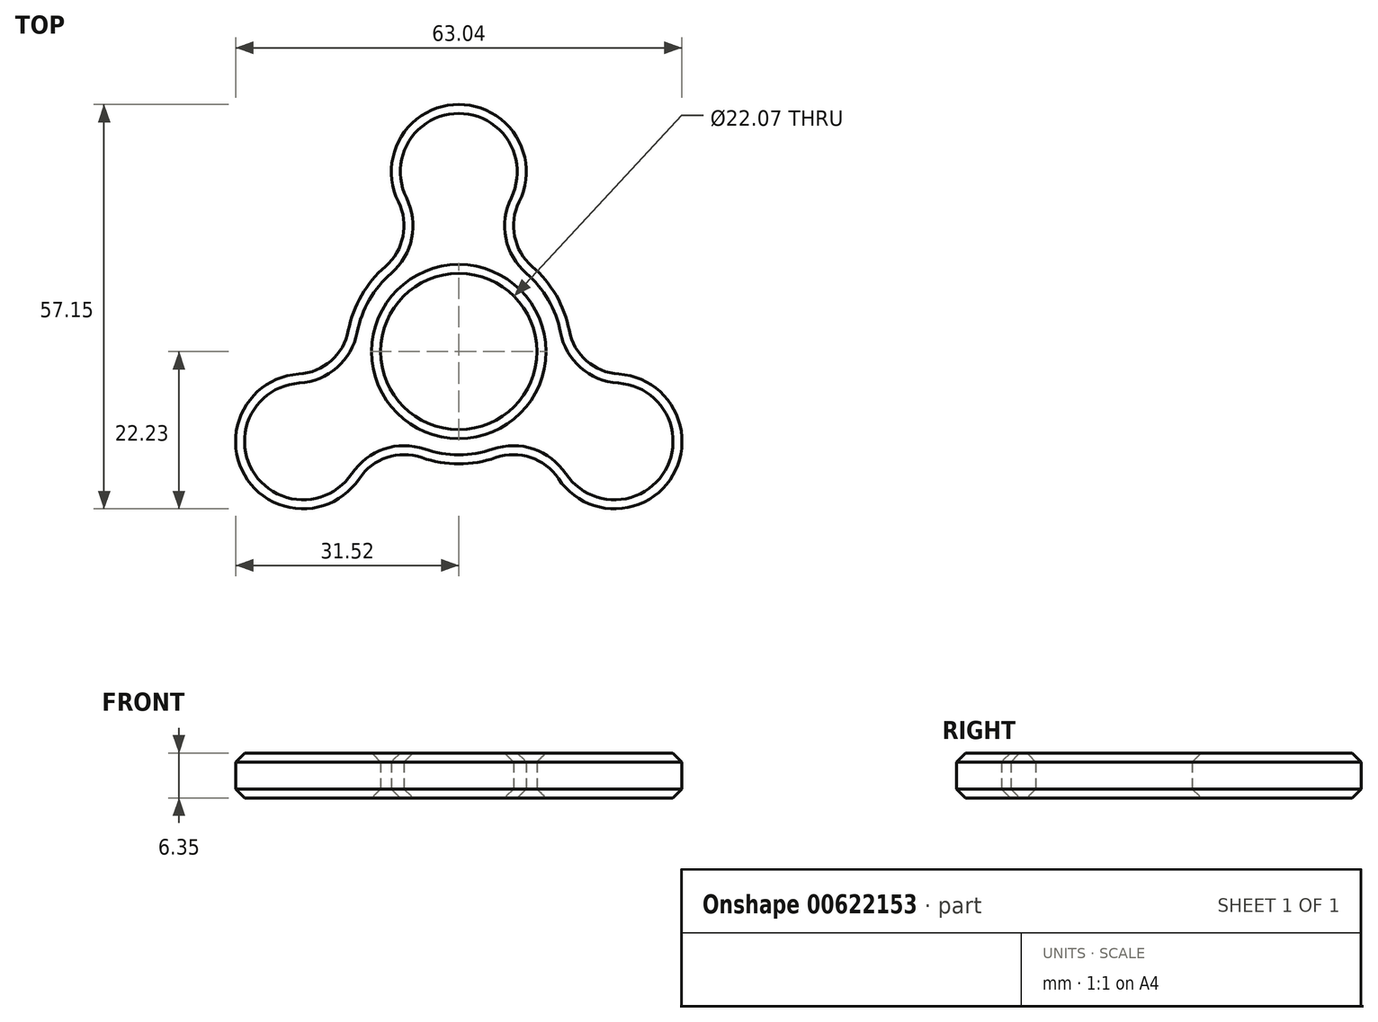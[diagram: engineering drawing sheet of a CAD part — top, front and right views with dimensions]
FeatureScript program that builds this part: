
annotation { "Feature Type Name" : "Feature", "Feature Type Description" : "" }
export const myFeature = defineFeature(function(context is Context, id is Id, definition is map)
    precondition{}
    {
        {
            var Q0;
            Q0=qCreatedBy(makeId("Top.planeOp"),FACE);
            var sketch = newSketch(context, id + "F0", { "sketchPlane" : qUnion([Q0])});
            skCircle(sketch, "E0", {"center": v(0, 0) * mm, "radius": 11.04 * mm});
            skCircle(sketch, "E1", {"center": v(0, 0) * mm, "radius": 15.88 * mm});
            skCircle(sketch, "E2", {"center": v(0, 25.4) * mm, "radius": 9.53 * mm});
            skCircle(sketch, "E3.1.0", {"center": v(-22, -12.7) * mm, "radius": 9.53 * mm});
            skCircle(sketch, "E3.2.0", {"center": v(22, -12.7) * mm, "radius": 9.53 * mm});
            skArc(sketch, "E4", {"start": v(-22.6, -3.2) * mm, "mid": v(-18.04, -1.3) * mm, "end": v(-15.6, 2.98) * mm});
            skArc(sketch, "E5", {"start": v(-5.22, -15) * mm, "mid": v(-10.15, -14.97) * mm, "end": v(-14.06, -17.97) * mm});
            skArc(sketch, "E6.1.0", {"start": v(14.06, -17.97) * mm, "mid": v(10.15, -14.97) * mm, "end": v(5.22, -15) * mm});
            skArc(sketch, "E6.1.1", {"start": v(15.6, 2.98) * mm, "mid": v(18.04, -1.3) * mm, "end": v(22.6, -3.2) * mm});
            skArc(sketch, "E6.2.0", {"start": v(8.53, 21.17) * mm, "mid": v(7.89, 16.27) * mm, "end": v(10.38, 12.01) * mm});
            skArc(sketch, "E6.2.1", {"start": v(-10.38, 12.01) * mm, "mid": v(-7.89, 16.27) * mm, "end": v(-8.53, 21.17) * mm});
            skSolve(sketch);
        }
        {
            var Q0;
            Q0 = qSketchRegion(id + "F0", true);
            var Q1;
            Q1=makeQuery(id+"F0.imprint","IMPRINT",FACE,{"disambiguationData":[TD([[makeQuery(id+"F0.imprint","IMPRINT",EDGE,{"derivedFrom":sQuery(id+"F0.wireOp",EDGE,"51Y64Ja3-wETz-725P-peQv-uXChOntkARGv")}),1.0]])]});
            extrude(context, id + "F1", {"entities" : qUnion([Q0, Q1]), "depth" : 6.35 * mm, "offsetDistance" : 25.4 * mm});
        }
        {
            var Q0;
            Q0=makeQuery(id+"F1.opExtrude","CAP_FACE",FACE,{"disambiguationData":[OSD([sQuery(id+"F0.wireOp",EDGE,"E0"),sQuery(id+"F0.wireOp",EDGE,"E1"),sQuery(id+"F0.wireOp",EDGE,"E2"),sQuery(id+"F0.wireOp",EDGE,"E3.1.0"),sQuery(id+"F0.wireOp",EDGE,"E3.2.0"),sQuery(id+"F0.wireOp",EDGE,"E4"),sQuery(id+"F0.wireOp",EDGE,"E5"),sQuery(id+"F0.wireOp",EDGE,"E6.1.0"),sQuery(id+"F0.wireOp",EDGE,"E6.1.1"),sQuery(id+"F0.wireOp",EDGE,"E6.2.0"),sQuery(id+"F0.wireOp",EDGE,"E6.2.1")])],"isStart":true});
            var Q1;
            Q1=makeQuery(id+"F1.opExtrude","CAP_FACE",FACE,{"disambiguationData":[OSD([sQuery(id+"F0.wireOp",EDGE,"E0"),sQuery(id+"F0.wireOp",EDGE,"E1"),sQuery(id+"F0.wireOp",EDGE,"E2"),sQuery(id+"F0.wireOp",EDGE,"E3.1.0"),sQuery(id+"F0.wireOp",EDGE,"E3.2.0"),sQuery(id+"F0.wireOp",EDGE,"E4"),sQuery(id+"F0.wireOp",EDGE,"E5"),sQuery(id+"F0.wireOp",EDGE,"E6.1.0"),sQuery(id+"F0.wireOp",EDGE,"E6.1.1"),sQuery(id+"F0.wireOp",EDGE,"E6.2.0"),sQuery(id+"F0.wireOp",EDGE,"E6.2.1")])],"isStart":false});
            chamfer(context, id + "F2", {"entities" : qUnion([Q0, Q1]), "width" : 1.27 * mm, "tangentPropagation" : true});
        }
    });
